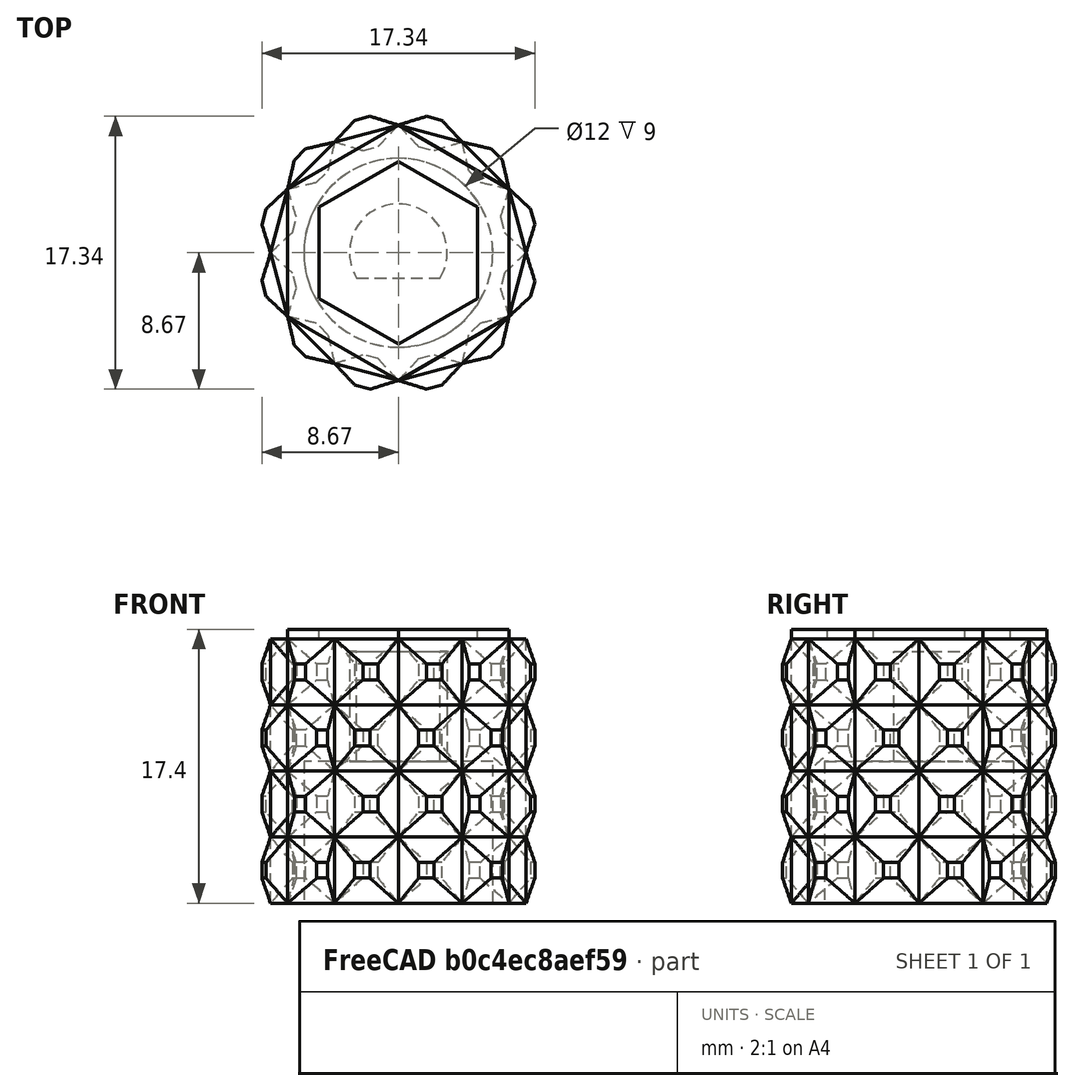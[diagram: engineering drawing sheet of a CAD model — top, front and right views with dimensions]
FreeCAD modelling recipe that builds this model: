
FCSTD DOCUMENT  (FreeCAD 1.0R38641 +678 (Git))
Label: Knob2
License: All rights reserved
LicenseURL: https://en.wikipedia.org/wiki/All_rights_reserved
objects: Sketcher::SketchObject×18, PartDesign::Pad×5, PartDesign::Pocket×5, PartDesign::AdditiveLoft×2, PartDesign::SubtractiveLoft×2, PartDesign::PolarPattern×1, PartDesign::LinearPattern×1, PartDesign::MultiTransform×1, PartDesign::Body×1, Mesh::Feature×1
note: 85 computed .brp shape members not serialized (recipe doc carries the construction recipe); baked Part::Feature solids carry a one-line shape summary decoded from their .brp

FEATURE [Sketcher::SketchObject] Sketch
  ArcFitTolerance = 0
  AttachmentSupport = -> [XY_Plane]
  FullyConstrained = true
  MakeInternals = false
  MapMode = 5
  sketch-geometry (5):
    g0: LineSegment StartX=0 StartY=0 StartZ=0 EndX=0 EndY=-8.11378 EndZ=0
    g1: LineSegment [constr] StartX=0 StartY=0 StartZ=0 EndX=4.05689 EndY=-7.02674 EndZ=0
    g2: LineSegment StartX=0 StartY=-8.11378 StartZ=0 EndX=4.05689 EndY=-7.02674 EndZ=0
    g3: LineSegment StartX=0 StartY=0 StartZ=0 EndX=7.02674 EndY=-4.05689 EndZ=0
    g4: LineSegment StartX=4.05689 StartY=-7.02674 StartZ=0 EndX=7.02674 EndY=-4.05689 EndZ=0
  constraints (13):
    c: Coincident(g0,g-1)
    c: PointOnObject(g0,g-2)
    c: Coincident(g1,g0)
    c: Equal(g0,g1)
    c: Coincident(g2,g0)
    c: Coincident(g1,g2)
    c: Angle(g0,g1) = 0.523599
    c: Coincident(g3,g0)
    c: Coincident(g4,g1)
    c: Coincident(g4,g3)
    c: Equal(g1,g3)
    c: Angle(g1,g3) = 0.523599
    c: Distance(g2) = 4.2
FEATURE [PartDesign::Pad] Pad
  Direction = (0,0,1)
  Length = 8.4
  Length2 = 10
  Profile = -> Sketch
  ReferenceAxis = -> Sketch [N_Axis]
  Suppressed = false
  Type = 0
FEATURE [Sketcher::SketchObject] Sketch001
  ArcFitTolerance = 0
  AttachmentSupport = -> [Pad]
  ExternalGeometry = -> [Pad]
  FullyConstrained = true
  MakeInternals = false
  MapMode = 5
  Placement = pos=(2.02844,-7.57026,0) rot=(0.983106,0.129428,0.129428;1.58783rad)
  sketch-geometry (4):
    g0: LineSegment StartX=-0.5 StartY=6.8 StartZ=0 EndX=0.5 EndY=6.8 EndZ=0
    g1: LineSegment StartX=0.5 StartY=6.8 StartZ=0 EndX=0.5 EndY=5.8 EndZ=0
    g2: LineSegment StartX=0.5 StartY=5.8 StartZ=0 EndX=-0.5 EndY=5.8 EndZ=0
    g3: LineSegment StartX=-0.5 StartY=5.8 StartZ=0 EndX=-0.5 EndY=6.8 EndZ=0
  constraints (12):
    c: Coincident(g0,g1)
    c: Coincident(g1,g2)
    c: Coincident(g2,g3)
    c: Coincident(g3,g0)
    c: Horizontal(g0)
    c: Horizontal(g2)
    c: Vertical(g1)
    c: Vertical(g3)
    c: DistanceX(g-4,g0) = 1.6
    c: DistanceX(g0,g-5) = 1.6
    c: DistanceY(g0,g-4) = 1.6
    c: DistanceY(g3,g3) = 1
FEATURE [PartDesign::Pad] Pad001
  BaseFeature = -> Pad
  Direction = (0.258819,-0.965926,0)
  Length = 1
  Length2 = 10
  Profile = -> Sketch001
  ReferenceAxis = -> Sketch001 [N_Axis]
  Suppressed = false
  Type = 0
FEATURE [Sketcher::SketchObject] Sketch002
  ArcFitTolerance = 0
  AttachmentSupport = -> [Pad001]
  ExternalGeometry = -> [Pad001]
  FullyConstrained = true
  MakeInternals = false
  MapMode = 5
  Placement = pos=(2.02844,-7.57026,0) rot=(0.983106,0.129428,0.129428;1.58783rad)
  sketch-geometry (4):
    g0: LineSegment StartX=-2.1 StartY=8.4 StartZ=0 EndX=2.1 EndY=8.4 EndZ=0
    g1: LineSegment StartX=2.1 StartY=8.4 StartZ=0 EndX=2.1 EndY=4.2 EndZ=0
    g2: LineSegment StartX=2.1 StartY=4.2 StartZ=0 EndX=-2.1 EndY=4.2 EndZ=0
    g3: LineSegment StartX=-2.1 StartY=4.2 StartZ=0 EndX=-2.1 EndY=8.4 EndZ=0
  constraints (10):
    c: Coincident(g0,g1)
    c: Coincident(g1,g2)
    c: Coincident(g2,g3)
    c: Coincident(g3,g0)
    c: Horizontal(g2)
    c: Vertical(g1)
    c: Vertical(g3)
    c: DistanceY(g3,g3) = 4.2
    c: Coincident(g0,g-5)
    c: Coincident(g0,g-4)
FEATURE [Sketcher::SketchObject] Sketch003
  ArcFitTolerance = 0
  AttachmentSupport = -> [Pad001]
  ExternalGeometry = -> [Pad001]
  FullyConstrained = true
  MakeInternals = false
  MapMode = 5
  Placement = pos=(2.28726,-8.53618,0) rot=(0.983106,0.129428,0.129428;1.58783rad)
  sketch-geometry (4):
    g0: LineSegment StartX=-0.5 StartY=6.8 StartZ=0 EndX=0.5 EndY=6.8 EndZ=0
    g1: LineSegment StartX=0.5 StartY=6.8 StartZ=0 EndX=0.5 EndY=5.8 EndZ=0
    g2: LineSegment StartX=0.5 StartY=5.8 StartZ=0 EndX=-0.5 EndY=5.8 EndZ=0
    g3: LineSegment StartX=-0.5 StartY=5.8 StartZ=0 EndX=-0.5 EndY=6.8 EndZ=0
  constraints (10):
    c: Coincident(g0,g1)
    c: Coincident(g1,g2)
    c: Coincident(g2,g3)
    c: Coincident(g3,g0)
    c: Horizontal(g0)
    c: Horizontal(g2)
    c: Vertical(g1)
    c: Vertical(g3)
    c: Coincident(g0,g-6)
    c: Coincident(g1,g-5)
FEATURE [PartDesign::AdditiveLoft] AdditiveLoft
  BaseFeature = -> Pad001
  Closed = false
  Profile = -> Sketch002
  Ruled = false
  Sections = -> [Sketch003]
  Suppressed = false
FEATURE [Sketcher::SketchObject] Sketch004
  ArcFitTolerance = 0
  AttachmentSupport = -> [AdditiveLoft]
  ExternalGeometry = -> [AdditiveLoft]
  FullyConstrained = true
  MakeInternals = false
  MapMode = 5
  Placement = pos=(2.02844,-7.57026,0) rot=(0.983106,0.129428,0.129428;1.58783rad)
  sketch-geometry (4):
    g0: LineSegment StartX=-0.5 StartY=2.6 StartZ=0 EndX=0.5 EndY=2.6 EndZ=0
    g1: LineSegment StartX=0.5 StartY=2.6 StartZ=0 EndX=0.5 EndY=1.6 EndZ=0
    g2: LineSegment StartX=0.5 StartY=1.6 StartZ=0 EndX=-0.5 EndY=1.6 EndZ=0
    g3: LineSegment StartX=-0.5 StartY=1.6 StartZ=0 EndX=-0.5 EndY=2.6 EndZ=0
  constraints (12):
    c: Coincident(g0,g1)
    c: Coincident(g1,g2)
    c: Coincident(g2,g3)
    c: Coincident(g3,g0)
    c: Horizontal(g0)
    c: Horizontal(g2)
    c: Vertical(g1)
    c: Vertical(g3)
    c: DistanceX(g-3,g2) = 1.6
    c: DistanceY(g-3,g2) = 1.6
    c: DistanceX(g1,g-4) = 1.6
    c: DistanceY(g3,g3) = 1
FEATURE [PartDesign::Pocket] Pocket
  BaseFeature = -> AdditiveLoft
  Direction = (-0.258819,0.965926,0)
  Length = 1
  Length2 = 5
  Profile = -> Sketch004
  ReferenceAxis = -> Sketch004 [N_Axis]
  Suppressed = false
  Type = 0
FEATURE [Sketcher::SketchObject] Sketch005
  ArcFitTolerance = 0
  AttachmentSupport = -> [Pocket]
  ExternalGeometry = -> [Pocket]
  FullyConstrained = true
  MakeInternals = false
  MapMode = 5
  Placement = pos=(2.02844,-7.57026,0) rot=(0.983106,0.129428,0.129428;1.58783rad)
  sketch-geometry (4):
    g0: LineSegment StartX=-2.1 StartY=4.2 StartZ=0 EndX=2.1 EndY=4.2 EndZ=0
    g1: LineSegment StartX=2.1 StartY=4.2 StartZ=0 EndX=2.1 EndY=0 EndZ=0
    g2: LineSegment StartX=2.1 StartY=0 StartZ=0 EndX=-2.1 EndY=0 EndZ=0
    g3: LineSegment StartX=-2.1 StartY=0 StartZ=0 EndX=-2.1 EndY=4.2 EndZ=0
  constraints (10):
    c: Coincident(g0,g1)
    c: Coincident(g1,g2)
    c: Coincident(g2,g3)
    c: Coincident(g3,g0)
    c: Horizontal(g0)
    c: Horizontal(g2)
    c: Vertical(g1)
    c: Vertical(g3)
    c: Coincident(g0,g-4)
    c: Coincident(g1,g-6)
FEATURE [Sketcher::SketchObject] Sketch006
  ArcFitTolerance = 0
  AttachmentSupport = -> [Pocket]
  ExternalGeometry = -> [Pocket]
  FullyConstrained = true
  MakeInternals = false
  MapMode = 5
  Placement = pos=(1.76963,-6.60433,0) rot=(0.983106,0.129428,0.129428;1.58783rad)
  sketch-geometry (4):
    g0: LineSegment StartX=-0.5 StartY=2.6 StartZ=0 EndX=0.5 EndY=2.6 EndZ=0
    g1: LineSegment StartX=0.5 StartY=2.6 StartZ=0 EndX=0.5 EndY=1.6 EndZ=0
    g2: LineSegment StartX=0.5 StartY=1.6 StartZ=0 EndX=-0.5 EndY=1.6 EndZ=0
    g3: LineSegment StartX=-0.5 StartY=1.6 StartZ=0 EndX=-0.5 EndY=2.6 EndZ=0
  constraints (10):
    c: Coincident(g0,g1)
    c: Coincident(g1,g2)
    c: Coincident(g2,g3)
    c: Coincident(g3,g0)
    c: Horizontal(g0)
    c: Horizontal(g2)
    c: Vertical(g1)
    c: Vertical(g3)
    c: Coincident(g0,g-4)
    c: Coincident(g1,g-6)
FEATURE [PartDesign::SubtractiveLoft] SubtractiveLoft
  BaseFeature = -> Pocket
  Closed = false
  Profile = -> Sketch006
  Ruled = false
  Sections = -> [Sketch005]
  Suppressed = false
FEATURE [Sketcher::SketchObject] Sketch007
  ArcFitTolerance = 0
  AttachmentSupport = -> [SubtractiveLoft]
  ExternalGeometry = -> [SubtractiveLoft]
  FullyConstrained = true
  MakeInternals = false
  MapMode = 5
  Placement = pos=(5.54181,-5.54181,0) rot=(0.862856,0.357407,0.357407;1.71777rad)
  sketch-geometry (4):
    g0: LineSegment StartX=-0.5 StartY=6.8 StartZ=0 EndX=0.5 EndY=6.8 EndZ=0
    g1: LineSegment StartX=0.5 StartY=6.8 StartZ=0 EndX=0.5 EndY=5.8 EndZ=0
    g2: LineSegment StartX=0.5 StartY=5.8 StartZ=0 EndX=-0.5 EndY=5.8 EndZ=0
    g3: LineSegment StartX=-0.5 StartY=5.8 StartZ=0 EndX=-0.5 EndY=6.8 EndZ=0
  constraints (12):
    c: Coincident(g0,g1)
    c: Coincident(g1,g2)
    c: Coincident(g2,g3)
    c: Coincident(g3,g0)
    c: Horizontal(g0)
    c: Horizontal(g2)
    c: Vertical(g1)
    c: Vertical(g3)
    c: DistanceX(g-4,g0) = 1.6
    c: DistanceX(g0,g-3) = 1.6
    c: DistanceY(g0,g-3) = 1.6
    c: DistanceY(g1,g1) = 1
FEATURE [PartDesign::Pocket] Pocket001
  BaseFeature = -> SubtractiveLoft
  Direction = (-0.707107,0.707107,1e-16)
  Length = 1
  Length2 = 5
  Profile = -> Sketch007
  ReferenceAxis = -> Sketch007 [N_Axis]
  Suppressed = false
  Type = 0
FEATURE [Sketcher::SketchObject] Sketch008
  ArcFitTolerance = 0
  AttachmentSupport = -> [Pocket001]
  ExternalGeometry = -> [Pocket001]
  FullyConstrained = true
  MakeInternals = false
  MapMode = 5
  Placement = pos=(5.54181,-5.54181,0) rot=(0.862856,0.357407,0.357407;1.71777rad)
  sketch-geometry (4):
    g0: LineSegment StartX=-2.1 StartY=8.4 StartZ=0 EndX=2.1 EndY=8.4 EndZ=0
    g1: LineSegment StartX=2.1 StartY=8.4 StartZ=0 EndX=2.1 EndY=4.2 EndZ=0
    g2: LineSegment StartX=2.1 StartY=4.2 StartZ=0 EndX=-2.1 EndY=4.2 EndZ=0
    g3: LineSegment StartX=-2.1 StartY=4.2 StartZ=0 EndX=-2.1 EndY=8.4 EndZ=0
  constraints (9):
    c: Coincident(g0,g1)
    c: Coincident(g1,g2)
    c: Coincident(g2,g3)
    c: Coincident(g3,g0)
    c: Horizontal(g2)
    c: Vertical(g1)
    c: Coincident(g0,g-4)
    c: Coincident(g2,g-3)
    c: Coincident(g-4,g0)
FEATURE [Sketcher::SketchObject] Sketch009
  ArcFitTolerance = 0
  AttachmentSupport = -> [Pocket001]
  ExternalGeometry = -> [Pocket001]
  FullyConstrained = true
  MakeInternals = false
  MapMode = 5
  Placement = pos=(4.83471,-4.83471,0) rot=(0.862856,0.357407,0.357407;1.71777rad)
  sketch-geometry (4):
    g0: LineSegment StartX=-0.5 StartY=6.8 StartZ=0 EndX=0.5 EndY=6.8 EndZ=0
    g1: LineSegment StartX=0.5 StartY=6.8 StartZ=0 EndX=0.5 EndY=5.8 EndZ=0
    g2: LineSegment StartX=0.5 StartY=5.8 StartZ=0 EndX=-0.5 EndY=5.8 EndZ=0
    g3: LineSegment StartX=-0.5 StartY=5.8 StartZ=0 EndX=-0.5 EndY=6.8 EndZ=0
  constraints (10):
    c: Coincident(g0,g1)
    c: Coincident(g1,g2)
    c: Coincident(g2,g3)
    c: Coincident(g3,g0)
    c: Horizontal(g0)
    c: Horizontal(g2)
    c: Vertical(g1)
    c: Vertical(g3)
    c: Coincident(g0,g-4)
    c: Coincident(g1,g-6)
FEATURE [PartDesign::SubtractiveLoft] SubtractiveLoft001
  BaseFeature = -> Pocket001
  Closed = false
  Profile = -> Sketch008
  Ruled = false
  Sections = -> [Sketch009]
  Suppressed = false
FEATURE [Sketcher::SketchObject] Sketch010
  ArcFitTolerance = 0
  AttachmentSupport = -> [SubtractiveLoft001]
  ExternalGeometry = -> [SubtractiveLoft001]
  FullyConstrained = true
  MakeInternals = false
  MapMode = 5
  Placement = pos=(5.54181,-5.54181,0) rot=(0.862856,0.357407,0.357407;1.71777rad)
  sketch-geometry (4):
    g0: LineSegment StartX=-0.5 StartY=2.6 StartZ=0 EndX=0.5 EndY=2.6 EndZ=0
    g1: LineSegment StartX=0.5 StartY=2.6 StartZ=0 EndX=0.5 EndY=1.6 EndZ=0
    g2: LineSegment StartX=0.5 StartY=1.6 StartZ=0 EndX=-0.5 EndY=1.6 EndZ=0
    g3: LineSegment StartX=-0.5 StartY=1.6 StartZ=0 EndX=-0.5 EndY=2.6 EndZ=0
  constraints (12):
    c: Coincident(g0,g1)
    c: Coincident(g1,g2)
    c: Coincident(g2,g3)
    c: Coincident(g3,g0)
    c: Horizontal(g0)
    c: Horizontal(g2)
    c: Vertical(g1)
    c: Vertical(g3)
    c: DistanceX(g-6,g2) = 1.6
    c: DistanceX(g1,g-6) = 1.6
    c: DistanceY(g-6,g1) = 1.6
    c: DistanceY(g1,g1) = 1
FEATURE [PartDesign::Pad] Pad002
  BaseFeature = -> SubtractiveLoft001
  Direction = (0.707107,-0.707107,-1e-16)
  Length = 1
  Length2 = 10
  Profile = -> Sketch010
  ReferenceAxis = -> Sketch010 [N_Axis]
  Suppressed = false
  Type = 0
FEATURE [Sketcher::SketchObject] Sketch011
  ArcFitTolerance = 0
  AttachmentSupport = -> [Pad002]
  ExternalGeometry = -> [Pad002]
  FullyConstrained = true
  MakeInternals = false
  MapMode = 5
  Placement = pos=(5.54181,-5.54181,0) rot=(0.862856,0.357407,0.357407;1.71777rad)
  sketch-geometry (4):
    g0: LineSegment StartX=-2.1 StartY=4.2 StartZ=0 EndX=2.1 EndY=4.2 EndZ=0
    g1: LineSegment StartX=2.1 StartY=4.2 StartZ=0 EndX=2.1 EndY=0 EndZ=0
    g2: LineSegment StartX=2.1 StartY=0 StartZ=0 EndX=-2.1 EndY=0 EndZ=0
    g3: LineSegment StartX=-2.1 StartY=0 StartZ=0 EndX=-2.1 EndY=4.2 EndZ=0
  constraints (10):
    c: Coincident(g0,g1)
    c: Coincident(g1,g2)
    c: Coincident(g2,g3)
    c: Coincident(g3,g0)
    c: Horizontal(g0)
    c: Horizontal(g2)
    c: Vertical(g1)
    c: Vertical(g3)
    c: Coincident(g0,g-4)
    c: Coincident(g1,g-6)
FEATURE [Sketcher::SketchObject] Sketch012
  ArcFitTolerance = 0
  AttachmentSupport = -> [Pad002]
  ExternalGeometry = -> [Pad002]
  FullyConstrained = true
  MakeInternals = false
  MapMode = 5
  Placement = pos=(6.24892,-6.24892,-2.7e-15) rot=(0.862856,0.357407,0.357407;1.71777rad)
  sketch-geometry (4):
    g0: LineSegment StartX=-0.5 StartY=2.6 StartZ=0 EndX=0.5 EndY=2.6 EndZ=0
    g1: LineSegment StartX=0.5 StartY=2.6 StartZ=0 EndX=0.5 EndY=1.6 EndZ=0
    g2: LineSegment StartX=0.5 StartY=1.6 StartZ=0 EndX=-0.5 EndY=1.6 EndZ=0
    g3: LineSegment StartX=-0.5 StartY=1.6 StartZ=0 EndX=-0.5 EndY=2.6 EndZ=0
  constraints (10):
    c: Coincident(g0,g1)
    c: Coincident(g1,g2)
    c: Coincident(g2,g3)
    c: Coincident(g3,g0)
    c: Horizontal(g0)
    c: Horizontal(g2)
    c: Vertical(g1)
    c: Vertical(g3)
    c: Coincident(g0,g-4)
    c: Coincident(g1,g-6)
FEATURE [PartDesign::AdditiveLoft] AdditiveLoft001
  BaseFeature = -> Pad002
  Closed = false
  Profile = -> Sketch011
  Ruled = false
  Sections = -> [Sketch012]
  Suppressed = false
FEATURE [PartDesign::PolarPattern] PolarPattern
  Angle = 360
  Axis = -> Sketch [N_Axis]
  Mode = 0
  Occurrences = 6
  Offset = 120
  Suppressed = false
  TransformMode = 0
FEATURE [PartDesign::LinearPattern] LinearPattern
  Direction = -> Z_Axis
  Length = 8.4
  Mode = 0
  Occurrences = 2
  Offset = 8.4
  Suppressed = false
  TransformMode = 0
FEATURE [PartDesign::MultiTransform] MultiTransform
  BaseFeature = -> AdditiveLoft001
  Originals = -> [Pad,Pad001,AdditiveLoft,Pocket,SubtractiveLoft,Pocket001,SubtractiveLoft001,Pad002,AdditiveLoft001]
  Suppressed = false
  TransformMode = 0
  Transformations = -> [PolarPattern,LinearPattern]
FEATURE [Sketcher::SketchObject] Sketch013
  ArcFitTolerance = 0
  AttachmentSupport = -> [MultiTransform]
  FullyConstrained = true
  MakeInternals = false
  MapMode = 5
  Placement = pos=(0,0,0) rot=(1,0,0;3.14159rad)
  sketch-geometry (1):
    g0: Circle CenterX=0 CenterY=0 CenterZ=0 NormalX=0 NormalY=0 NormalZ=1 AngleXU=0 Radius=6
  constraints (2):
    c: Coincident(g0,g-1)
    c: Diameter(g0) = 12
FEATURE [PartDesign::Pocket] Pocket002
  BaseFeature = -> MultiTransform
  Direction = (0,0,1)
  Length = 9
  Length2 = 5
  Profile = -> Sketch013
  ReferenceAxis = -> Sketch013 [N_Axis]
  Suppressed = false
  Type = 0
FEATURE [Sketcher::SketchObject] Sketch014
  ArcFitTolerance = 0
  AttachmentSupport = -> [Pocket002]
  FullyConstrained = true
  MakeInternals = false
  MapMode = 5
  Placement = pos=(0,0,9) rot=(1,0,0;3.14159rad)
  sketch-geometry (2):
    g0: LineSegment StartX=-2.65518 StartY=1.6 StartZ=0 EndX=2.65518 EndY=1.6 EndZ=0
    g1: ArcOfCircle CenterX=0 CenterY=0 CenterZ=0 NormalX=0 NormalY=0 NormalZ=1 AngleXU=0 Radius=3.1 StartAngle=2.59927 EndAngle=6.82551
  constraints (6):
    c: Horizontal(g0)
    c: Coincident(g1,g-1)
    c: Coincident(g1,g0)
    c: Coincident(g1,g0)
    c: Radius(g1) = 3.1
    c: DistanceY(g1,g0) = 1.6
FEATURE [PartDesign::Pocket] Pocket003
  BaseFeature = -> Pocket002
  Direction = (0,0,1)
  Length = 7
  Length2 = 5
  Profile = -> Sketch014
  ReferenceAxis = -> Sketch014 [N_Axis]
  Suppressed = false
  Type = 0
FEATURE [Sketcher::SketchObject] Sketch015
  ArcFitTolerance = 0
  AttachmentSupport = -> [Pocket003]
  ExternalGeometry = -> [Pocket003]
  FullyConstrained = true
  MakeInternals = false
  MapMode = 5
  Placement = pos=(0,0,16.8) rot=(0,0,1;0rad)
  sketch-geometry (12):
    g0: LineSegment StartX=-7.02674 StartY=4.05689 StartZ=0 EndX=4.4e-15 EndY=8.11378 EndZ=0
    g1: LineSegment StartX=-7.02674 StartY=4.05689 StartZ=0 EndX=-7.02674 EndY=-4.05689 EndZ=0
    g2: LineSegment StartX=-5.02674 StartY=2.90219 StartZ=0 EndX=5.3e-15 EndY=5.80438 EndZ=0
    g3: LineSegment StartX=5.3e-15 StartY=5.80438 StartZ=0 EndX=5.02674 EndY=2.90219 EndZ=0
    g4: LineSegment StartX=5.02674 StartY=2.90219 StartZ=0 EndX=5.02674 EndY=-2.90219 EndZ=0
    g5: LineSegment StartX=5.02674 StartY=-2.90219 StartZ=0 EndX=0 EndY=-5.80438 EndZ=0
    g6: LineSegment StartX=0 StartY=-5.80438 StartZ=0 EndX=-5.02674 EndY=-2.90219 EndZ=0
    g7: LineSegment StartX=-5.02674 StartY=-2.90219 StartZ=0 EndX=-5.02674 EndY=2.90219 EndZ=0
    g8: LineSegment StartX=-7.02674 StartY=-4.05689 StartZ=0 EndX=9e-16 EndY=-8.11378 EndZ=0
    g9: LineSegment StartX=9e-16 StartY=-8.11378 StartZ=0 EndX=7.02674 EndY=-4.05689 EndZ=0
    g10: LineSegment StartX=4.4e-15 StartY=8.11378 StartZ=0 EndX=7.02674 EndY=4.05689 EndZ=0
    g11: LineSegment StartX=7.02674 StartY=4.05689 StartZ=0 EndX=7.02674 EndY=-4.05689 EndZ=0
  constraints (30):
    c: Coincident(g0,g-3)
    c: Coincident(g1,g0)
    c: Coincident(g3,g2)
    c: Coincident(g4,g3)
    c: Coincident(g5,g4)
    c: Coincident(g6,g5)
    c: Coincident(g7,g6)
    c: Coincident(g7,g2)
    c: Parallel(g2,g0)
    c: Coincident(g8,g1)
    c: Coincident(g8,g-4)
    c: Coincident(g9,g8)
    c: Coincident(g10,g-5)
    c: Coincident(g11,g10)
    c: Parallel(g3,g10)
    c: Parallel(g4,g11)
    c: Parallel(g5,g9)
    c: Parallel(g6,g8)
    c: Distance(g2,g0) = 2
    c: Coincident(g10,g-7)
    c: Coincident(g0,g10)
    c: Coincident(g1,g-15)
    c: Coincident(g11,g-11)
    c: Coincident(g9,g11)
    c: Distance(g10,g3) = 2
    c: Parallel(g7,g1)
    c: Distance(g1,g7) = 2
    c: Distance(g8,g6) = 2
    c: Distance(g9,g5) = 2
    c: Distance(g11,g4) = 2
FEATURE [PartDesign::Pad] Pad003
  BaseFeature = -> Pocket003
  Direction = (0,0,1)
  Length = 0.6
  Length2 = 10
  Profile = -> Sketch015
  ReferenceAxis = -> Sketch015 [N_Axis]
  Suppressed = false
  Type = 0
FEATURE [Sketcher::SketchObject] Sketch016
  ArcFitTolerance = 0
  AttachmentSupport = -> [Pad003]
  FullyConstrained = true
  MakeInternals = false
  MapMode = 5
  Placement = pos=(0,0,0) rot=(1,0,0;3.14159rad)
  sketch-geometry (1):
    g0: Circle CenterX=0 CenterY=0 CenterZ=0 NormalX=0 NormalY=0 NormalZ=1 AngleXU=0 Radius=12
  constraints (2):
    c: Coincident(g0,g-1)
    c: Diameter(g0) = 24
FEATURE [PartDesign::Pocket] Pocket004
  BaseFeature = -> Pad003
  Direction = (0,0,1)
  Length = 4.2
  Length2 = 5
  Profile = -> Sketch016
  ReferenceAxis = -> Sketch016 [N_Axis]
  Suppressed = false
  Type = 0
FEATURE [Sketcher::SketchObject] Sketch017
  ArcFitTolerance = 0
  AttachmentSupport = -> [Pocket004]
  FullyConstrained = true
  MakeInternals = false
  MapMode = 5
  Placement = pos=(0,0,4.2) rot=(1,0,0;3.14159rad)
  sketch-geometry (2):
    g0: Circle CenterX=0 CenterY=0 CenterZ=0 NormalX=0 NormalY=0 NormalZ=1 AngleXU=0 Radius=9.25
    g1: Circle CenterX=0 CenterY=0 CenterZ=0 NormalX=0 NormalY=0 NormalZ=1 AngleXU=0 Radius=6
  constraints (4):
    c: Coincident(g0,g-1)
    c: Diameter(g0) = 18.5
    c: Coincident(g1,g0)
    c: Diameter(g1) = 12
FEATURE [PartDesign::Pad] Pad004
  BaseFeature = -> Pocket004
  Direction = (0,0,-1)
  Length = 3.6
  Length2 = 10
  Profile = -> Sketch017
  ReferenceAxis = -> Sketch017 [N_Axis]
  Reversed = true
  Suppressed = false
  Type = 0
FEATURE [PartDesign::Body] Body
  AllowCompound = false
  Group = -> [Sketch,Pad,Sketch001,Pad001,Sketch002,Sketch003,AdditiveLoft,Sketch004,Pocket,Sketch005,Sketch006,SubtractiveLoft,Sketch007,Pocket001,Sketch008,Sketch009,SubtractiveLoft001,Sketch010,Pad002,Sketch011,Sketch012,AdditiveLoft001,MultiTransform,PolarPattern,LinearPattern,Sketch013,Pocket002,Sketch014,Pocket003,Sketch015,Pad003,Sketch016,Pocket004,Sketch017,Pad004]
  Origin = -> Origin
  Tip = -> Pad003
FEATURE [Mesh::Feature] Mesh  label="Knob2 (Meshed)"
